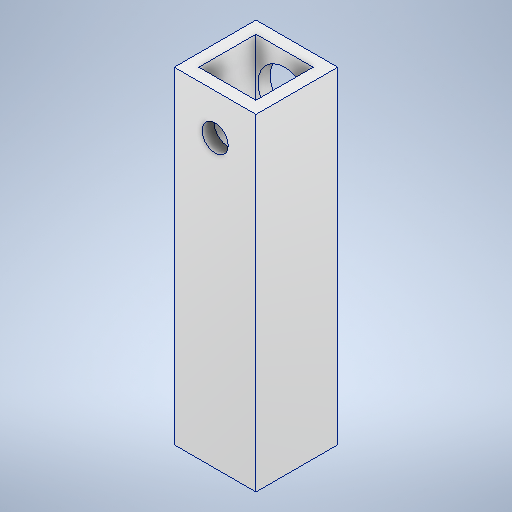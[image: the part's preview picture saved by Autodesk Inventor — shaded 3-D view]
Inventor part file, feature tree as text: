
AUTODESK INVENTOR PART (.ipt)
format: ipt  version: 2025 (Build 290162000, 162)  size: 271,872 bytes
history: native  units: mm
features: sketch x3, hole x2, other x1, extrude x1
ambient origin geometry x8: Origin, YZ Plane, XZ Plane, XY Plane, X Axis, Y Axis, Z Axis, Center Point
bodies: Body1 (feature_tree)
feature tree (7):
  other  "Těleso1"
  extrude  "Vysunutí1"  Depth=10.0mm
  hole  "Díra1"  [1 undecoded]
  hole  "Díra2"  [1 undecoded]
  sketch  "Náčrt1"
  sketch  "Náčrt2"
  sketch  "Náčrt3"
note: 2 required parameter values undecoded (feature->parameter linkage not recoverable at this tier; creation-order binding heuristic only, values carry confidence <= 0.55)
